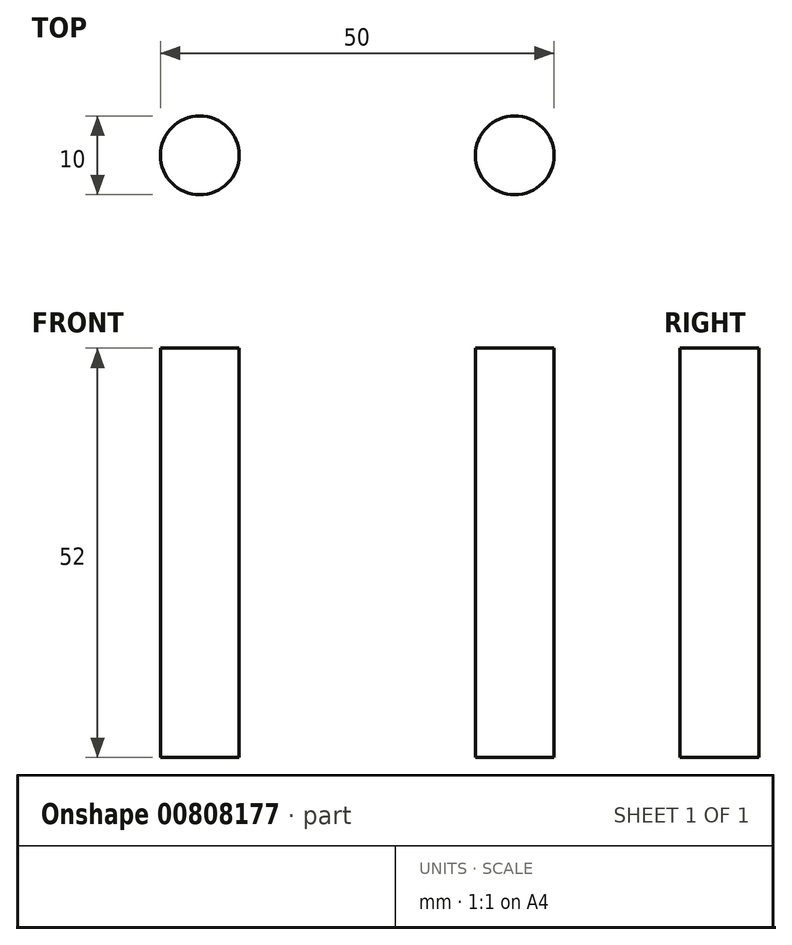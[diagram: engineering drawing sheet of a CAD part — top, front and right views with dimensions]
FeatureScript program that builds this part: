
annotation { "Feature Type Name" : "Feature", "Feature Type Description" : "" }
export const myFeature = defineFeature(function(context is Context, id is Id, definition is map)
    precondition{}
    {
        {
            var Q0;
            Q0=qCreatedBy(makeId("Top.planeOp"),FACE);
            var sketch = newSketch(context, id + "F0", { "sketchPlane" : qUnion([Q0])});
            skLineSegment(sketch, "E0.bottom", {"start": v(-25, 25) * mm, "end": v(25, 25) * mm});
            skLineSegment(sketch, "E0.top", {"start": v(-25, -25) * mm, "end": v(25, -25) * mm});
            skLineSegment(sketch, "E0.left", {"start": v(-25, 25) * mm, "end": v(-25, -25) * mm});
            skLineSegment(sketch, "E0.right", {"start": v(25, 25) * mm, "end": v(25, -25) * mm});
            skPoint(sketch, "E0.middle", {"position": v(0, 0) * mm});
            skLineSegment(sketch, "E1.bottom", {"start": v(-25, 25) * mm, "end": v(-15, 25) * mm});
            skLineSegment(sketch, "E1.top", {"start": v(-25, 15) * mm, "end": v(-15, 15) * mm});
            skLineSegment(sketch, "E1.left", {"start": v(-25, 25) * mm, "end": v(-25, 15) * mm});
            skLineSegment(sketch, "E1.right", {"start": v(-15, 25) * mm, "end": v(-15, 15) * mm});
            skLineSegment(sketch, "E2.bottom", {"start": v(-25, -25) * mm, "end": v(-15, -25) * mm});
            skLineSegment(sketch, "E2.top", {"start": v(-25, -15) * mm, "end": v(-15, -15) * mm});
            skLineSegment(sketch, "E2.left", {"start": v(-25, -25) * mm, "end": v(-25, -15) * mm});
            skLineSegment(sketch, "E2.right", {"start": v(-15, -25) * mm, "end": v(-15, -15) * mm});
            skLineSegment(sketch, "E3.bottom", {"start": v(25, -25) * mm, "end": v(15, -25) * mm});
            skLineSegment(sketch, "E3.top", {"start": v(25, -15) * mm, "end": v(15, -15) * mm});
            skLineSegment(sketch, "E3.left", {"start": v(25, -25) * mm, "end": v(25, -15) * mm});
            skLineSegment(sketch, "E3.right", {"start": v(15, -25) * mm, "end": v(15, -15) * mm});
            skLineSegment(sketch, "E4.bottom", {"start": v(25, 25) * mm, "end": v(15, 25) * mm});
            skLineSegment(sketch, "E4.top", {"start": v(25, 15) * mm, "end": v(15, 15) * mm});
            skLineSegment(sketch, "E4.left", {"start": v(25, 25) * mm, "end": v(25, 15) * mm});
            skLineSegment(sketch, "E4.right", {"start": v(15, 25) * mm, "end": v(15, 15) * mm});
            skPoint(sketch, "E5.visualSharp", {"position": v(-15, 15) * mm});
            skLineSegment(sketch, "E5.filletArc", {"start": v(-15, 15) * mm, "end": v(-15, 15) * mm});
            skPoint(sketch, "E6.visualSharp", {"position": v(-15, -15) * mm});
            skLineSegment(sketch, "E6.filletArc", {"start": v(-15, -15) * mm, "end": v(-15, -15) * mm});
            skPoint(sketch, "E7.visualSharp", {"position": v(15, -15) * mm});
            skLineSegment(sketch, "E7.filletArc", {"start": v(15, -15) * mm, "end": v(15, -15) * mm});
            skPoint(sketch, "E8.visualSharp", {"position": v(15, 15) * mm});
            skLineSegment(sketch, "E8.filletArc", {"start": v(15, 15) * mm, "end": v(15, 15) * mm});
            skSolve(sketch);
        }
        {
            var Q0;
            Q0=makeQuery(id+"F0.imprint","IMPRINT",FACE,{"disambiguationData":[TD([[makeQuery(id+"F0.imprint","IMPRINT",EDGE,{"derivedFrom":sQuery(id+"F0.wireOp",EDGE,"E0.bottom")}),-1.0]])]});
            extrude(context, id + "F1", {"entities" : qUnion([Q0]), "depth" : 52 * mm, "offsetDistance" : 25 * mm});
        }
        {
            var Q0;
            Q0=makeQuery(id+"F1.opExtrude","SWEPT_EDGE",EDGE,{"disambiguationData":[OSD([sQuery(id+"F0.wireOp",EDGE,"E2.top"),sQuery(id+"F0.wireOp",EDGE,"E2.right")])]});
            var Q1;
            Q1=makeQuery(id+"F1.opExtrude","SWEPT_EDGE",EDGE,{"disambiguationData":[OSD([sQuery(id+"F0.wireOp",EDGE,"E3.top"),sQuery(id+"F0.wireOp",EDGE,"E3.right")])]});
            var Q2;
            Q2=makeQuery(id+"F1.opExtrude","SWEPT_EDGE",EDGE,{"disambiguationData":[OSD([sQuery(id+"F0.wireOp",EDGE,"E4.top"),sQuery(id+"F0.wireOp",EDGE,"E4.right")])]});
            var Q3;
            Q3=makeQuery(id+"F1.opExtrude","SWEPT_EDGE",EDGE,{"disambiguationData":[OSD([sQuery(id+"F0.wireOp",EDGE,"E1.top"),sQuery(id+"F0.wireOp",EDGE,"E1.right")])]});
            fillet(context, id + "F2", {"entities" : qUnion([Q0, Q1, Q2, Q3]), "radius" : 5 * mm, "tangentPropagation" : true, "allowEdgeOverflow" : false});
        }
        {
            var Q0;
            Q0=makeQuery(id+"F1.opExtrude","SWEPT_EDGE",EDGE,{"disambiguationData":[OSD([sQuery(id+"F0.wireOp",EDGE,"E0.right"),sQuery(id+"F0.wireOp",EDGE,"E4.top"),sQuery(id+"F0.wireOp",EDGE,"E4.left")])]});
            var Q1;
            Q1=makeQuery(id+"F1.opExtrude","SWEPT_EDGE",EDGE,{"disambiguationData":[OSD([sQuery(id+"F0.wireOp",EDGE,"E0.bottom"),sQuery(id+"F0.wireOp",EDGE,"E1.bottom"),sQuery(id+"F0.wireOp",EDGE,"E1.right")])]});
            var Q2;
            Q2=makeQuery(id+"F1.opExtrude","SWEPT_EDGE",EDGE,{"disambiguationData":[OSD([sQuery(id+"F0.wireOp",EDGE,"E0.left"),sQuery(id+"F0.wireOp",EDGE,"E1.top"),sQuery(id+"F0.wireOp",EDGE,"E1.left")])]});
            var Q3;
            Q3=makeQuery(id+"F1.opExtrude","SWEPT_EDGE",EDGE,{"disambiguationData":[OSD([sQuery(id+"F0.wireOp",EDGE,"E0.right"),sQuery(id+"F0.wireOp",EDGE,"E3.top"),sQuery(id+"F0.wireOp",EDGE,"E3.left")])]});
            var Q4;
            Q4=makeQuery(id+"F1.opExtrude","SWEPT_EDGE",EDGE,{"disambiguationData":[OSD([sQuery(id+"F0.wireOp",EDGE,"E0.top"),sQuery(id+"F0.wireOp",EDGE,"E3.bottom"),sQuery(id+"F0.wireOp",EDGE,"E3.right")])]});
            var Q5;
            Q5=makeQuery(id+"F1.opExtrude","SWEPT_EDGE",EDGE,{"disambiguationData":[OSD([sQuery(id+"F0.wireOp",EDGE,"E0.top"),sQuery(id+"F0.wireOp",EDGE,"E2.bottom"),sQuery(id+"F0.wireOp",EDGE,"E2.right")])]});
            var Q6;
            Q6=makeQuery(id+"F1.opExtrude","SWEPT_EDGE",EDGE,{"disambiguationData":[OSD([sQuery(id+"F0.wireOp",EDGE,"E0.left"),sQuery(id+"F0.wireOp",EDGE,"E2.top"),sQuery(id+"F0.wireOp",EDGE,"E2.left")])]});
            var Q7;
            Q7=makeQuery(id+"F1.opExtrude","SWEPT_EDGE",EDGE,{"disambiguationData":[OSD([sQuery(id+"F0.wireOp",EDGE,"E0.bottom"),sQuery(id+"F0.wireOp",EDGE,"E4.bottom"),sQuery(id+"F0.wireOp",EDGE,"E4.right")])]});
            fillet(context, id + "F3", {"entities" : qUnion([Q0, Q1, Q2, Q3, Q4, Q5, Q6, Q7]), "radius" : 5 * mm, "tangentPropagation" : true, "allowEdgeOverflow" : false});
        }
    });
